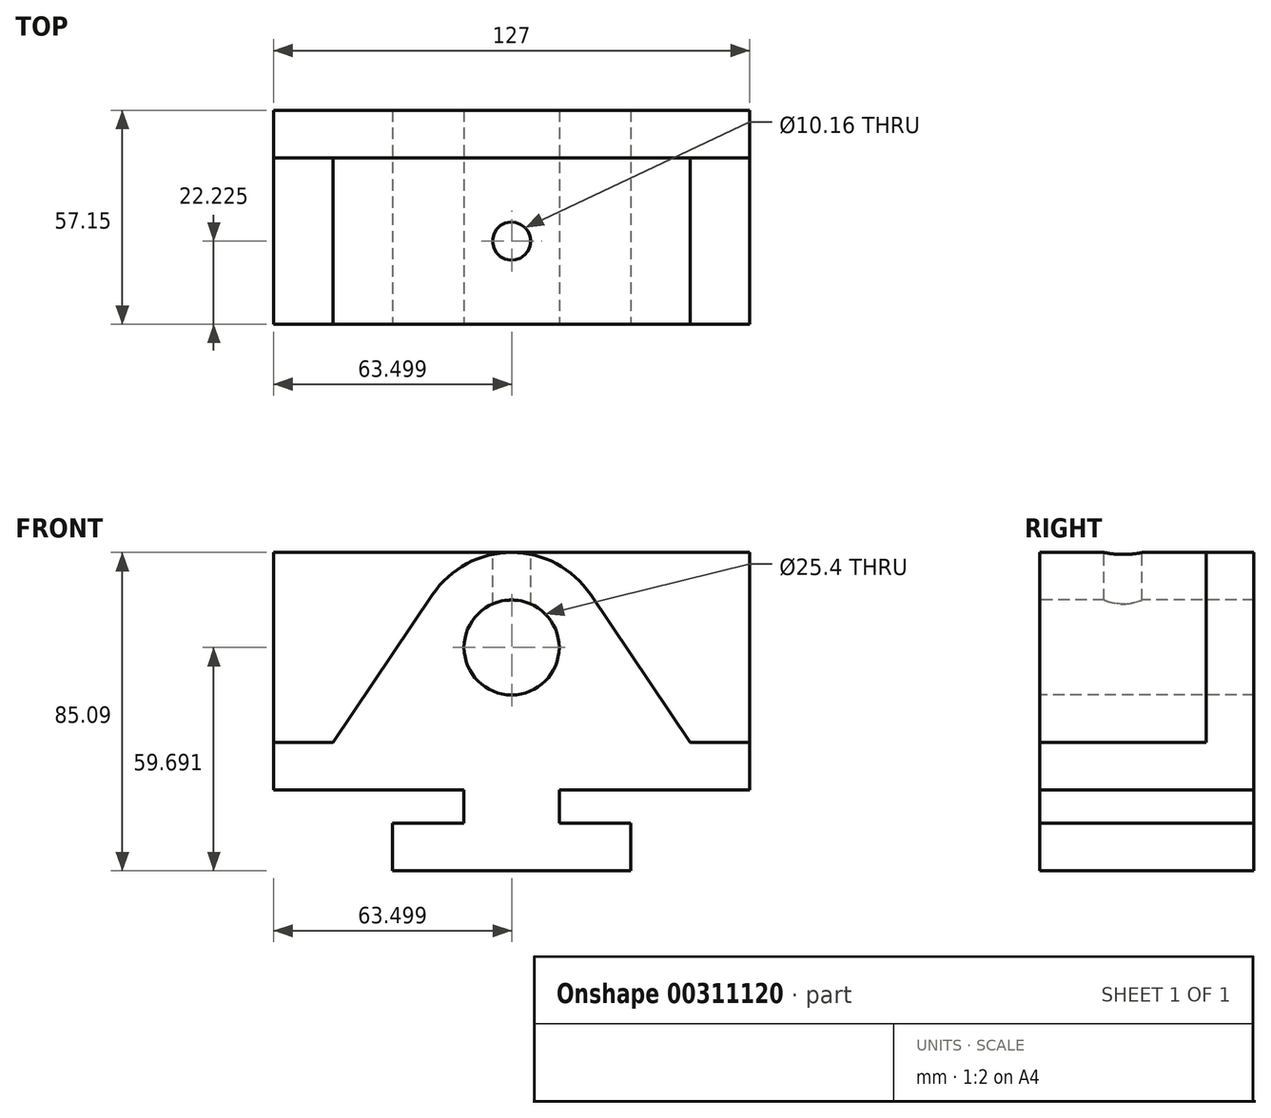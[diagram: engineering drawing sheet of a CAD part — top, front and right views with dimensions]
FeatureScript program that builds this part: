
annotation { "Feature Type Name" : "Feature", "Feature Type Description" : "" }
export const myFeature = defineFeature(function(context is Context, id is Id, definition is map)
    precondition{}
    {
        {
            var Q0;
            Q0=qCreatedBy(makeId("Front.planeOp"),FACE);
            var sketch = newSketch(context, id + "F0", { "sketchPlane" : qUnion([Q0])});
            skLineSegment(sketch, "E0.bottom", {"start": v(-85.18, 91.2) * mm, "end": v(41.82, 91.2) * mm});
            skLineSegment(sketch, "E0.top", {"start": v(-85.18, 6.11) * mm, "end": v(41.82, 6.11) * mm});
            skLineSegment(sketch, "E0.left", {"start": v(-85.18, 91.2) * mm, "end": v(-85.18, 6.11) * mm});
            skLineSegment(sketch, "E0.right", {"start": v(41.82, 91.2) * mm, "end": v(41.82, 6.11) * mm});
            skSolve(sketch);
        }
        {
            var Q0;
            Q0 = qSketchRegion(id + "F0", true);
            extrude(context, id + "F1", {"entities" : qUnion([Q0]), "oppositeDirection" : true, "depth" : 57.15 * mm});
        }
        {
            var Q0;
            Q0=makeQuery(id+"F1.opExtrude","CAP_FACE",FACE,{"disambiguationData":[OSD([sQuery(id+"F0.wireOp",EDGE,"E0.bottom"),sQuery(id+"F0.wireOp",EDGE,"E0.top"),sQuery(id+"F0.wireOp",EDGE,"E0.left"),sQuery(id+"F0.wireOp",EDGE,"E0.right")])],"isStart":true});
            var sketch = newSketch(context, id + "F2", { "sketchPlane" : qUnion([Q0])});
            skLineSegment(sketch, "E1", {"start": v(-21.68, 6.11) * mm, "end": v(10.07, 6.11) * mm});
            skLineSegment(sketch, "E2", {"start": v(10.07, 6.11) * mm, "end": v(10.07, 18.81) * mm});
            skLineSegment(sketch, "E3", {"start": v(10.07, 18.81) * mm, "end": v(-8.98, 18.81) * mm});
            skLineSegment(sketch, "E4", {"start": v(-8.98, 18.81) * mm, "end": v(-8.98, 27.7) * mm});
            skLineSegment(sketch, "E5", {"start": v(-8.98, 27.7) * mm, "end": v(41.82, 27.7) * mm});
            skLineSegment(sketch, "E6", {"start": v(41.82, 27.7) * mm, "end": v(41.82, 40.4) * mm});
            skLineSegment(sketch, "E7", {"start": v(41.82, 40.4) * mm, "end": v(25.94, 40.4) * mm});
            skLineSegment(sketch, "E8", {"start": v(25.94, 40.4) * mm, "end": v(-0.59, 79.95) * mm});
            skArc(sketch, "E9", {"start": v(-0.59, 79.95) * mm, "mid": v(-21.68, 91.2) * mm, "end": v(-42.77, 79.95) * mm});
            skLineSegment(sketch, "E10", {"start": v(-21.68, 6.11) * mm, "end": v(-53.43, 6.11) * mm});
            skLineSegment(sketch, "E11", {"start": v(-53.43, 6.11) * mm, "end": v(-53.43, 18.81) * mm});
            skLineSegment(sketch, "E12", {"start": v(-53.43, 18.81) * mm, "end": v(-34.38, 18.81) * mm});
            skLineSegment(sketch, "E13", {"start": v(-34.38, 18.81) * mm, "end": v(-34.38, 27.7) * mm});
            skLineSegment(sketch, "E14", {"start": v(-34.38, 27.7) * mm, "end": v(-85.18, 27.7) * mm});
            skLineSegment(sketch, "E15", {"start": v(-85.18, 27.7) * mm, "end": v(-85.18, 40.4) * mm});
            skLineSegment(sketch, "E16", {"start": v(-85.18, 40.4) * mm, "end": v(-69.3, 40.4) * mm});
            skLineSegment(sketch, "E17", {"start": v(-69.3, 40.4) * mm, "end": v(-42.77, 79.95) * mm});
            skCircle(sketch, "E18", {"center": v(-21.68, 65.8) * mm, "radius": 12.7 * mm});
            skSolve(sketch);
        }
        {
            var Q0;
            Q0=makeQuery(id+"F1.opExtrude","SWEPT_FACE",FACE,{"disambiguationData":[OSD([sQuery(id+"F0.wireOp",EDGE,"E0.bottom")])]});
            var sketch = newSketch(context, id + "F3", { "sketchPlane" : qUnion([Q0])});
            skCircle(sketch, "E19", {"center": v(-21.68, 22.23) * mm, "radius": 5.08 * mm});
            skPoint(sketch, "E19.centerSnap0", {"position": v(-21.68, 0) * mm});
            skSolve(sketch);
        }
        {
            var Q0;
            {var subQ4=sQuery(id+"F2.wireOp",EDGE,"E11");Q0=makeQuery(id+"F2.imprint","IMPRINT",FACE,{"disambiguationData":[TD([[makeQuery(id+"F2.imprint","IMPRINT",EDGE,{"derivedFrom":subQ4}),1.0]])]});}
            var Q1;
            {var subQ4=sQuery(id+"F2.wireOp",EDGE,"E2");Q1=makeQuery(id+"F2.imprint","IMPRINT",FACE,{"disambiguationData":[TD([[makeQuery(id+"F2.imprint","IMPRINT",EDGE,{"derivedFrom":subQ4}),-1.0]])]});}
            extrude(context, id + "F4", {"entities" : qUnion([Q0, Q1]), "operationType" : NewBodyOperationType.REMOVE, "endBound" : BoundingType.THROUGH_ALL, "oppositeDirection" : true, "depth" : 25.4 * mm});
        }
        {
            var Q0;
            {var subQ1=sQuery(id+"F2.wireOp",EDGE,"E16");Q0=makeQuery(id+"F2.imprint","IMPRINT",FACE,{"disambiguationData":[TD([[makeQuery(id+"F2.imprint","IMPRINT",EDGE,{"derivedFrom":subQ1}),1.0]])]});}
            var Q1;
            {var subQ6=sQuery(id+"F2.wireOp",EDGE,"E7");Q1=makeQuery(id+"F2.imprint","IMPRINT",FACE,{"disambiguationData":[TD([[makeQuery(id+"F2.imprint","IMPRINT",EDGE,{"derivedFrom":subQ6}),-1.0]])]});}
            extrude(context, id + "F5", {"entities" : qUnion([Q0, Q1]), "operationType" : NewBodyOperationType.REMOVE, "oppositeDirection" : true, "depth" : 44.45 * mm});
        }
        {
            var Q0;
            Q0=makeQuery(id+"F2.imprint","IMPRINT",FACE,{"disambiguationData":[TD([[makeQuery(id+"F2.imprint","IMPRINT",EDGE,{"derivedFrom":sQuery(id+"F2.wireOp",EDGE,"E18")}),1.0]])]});
            extrude(context, id + "F6", {"entities" : qUnion([Q0]), "operationType" : NewBodyOperationType.REMOVE, "endBound" : BoundingType.THROUGH_ALL, "oppositeDirection" : true, "depth" : 25.4 * mm});
        }
        {
            var Q0;
            Q0=makeQuery(id+"F3.imprint","IMPRINT",FACE,{"disambiguationData":[TD([[makeQuery(id+"F3.imprint","IMPRINT",EDGE,{"derivedFrom":sQuery(id+"F3.wireOp",EDGE,"E19")}),1.0]])]});
            var Q1;
            Q1=sQuery(id+"F3.wireOp",EDGE,"E19");
            extrude(context, id + "F7", {"entities" : qUnion([Q0]), "operationType" : NewBodyOperationType.REMOVE, "surfaceEntities" : qUnion([Q1]), "oppositeDirection" : true, "depth" : 25.4 * mm});
        }
    });
